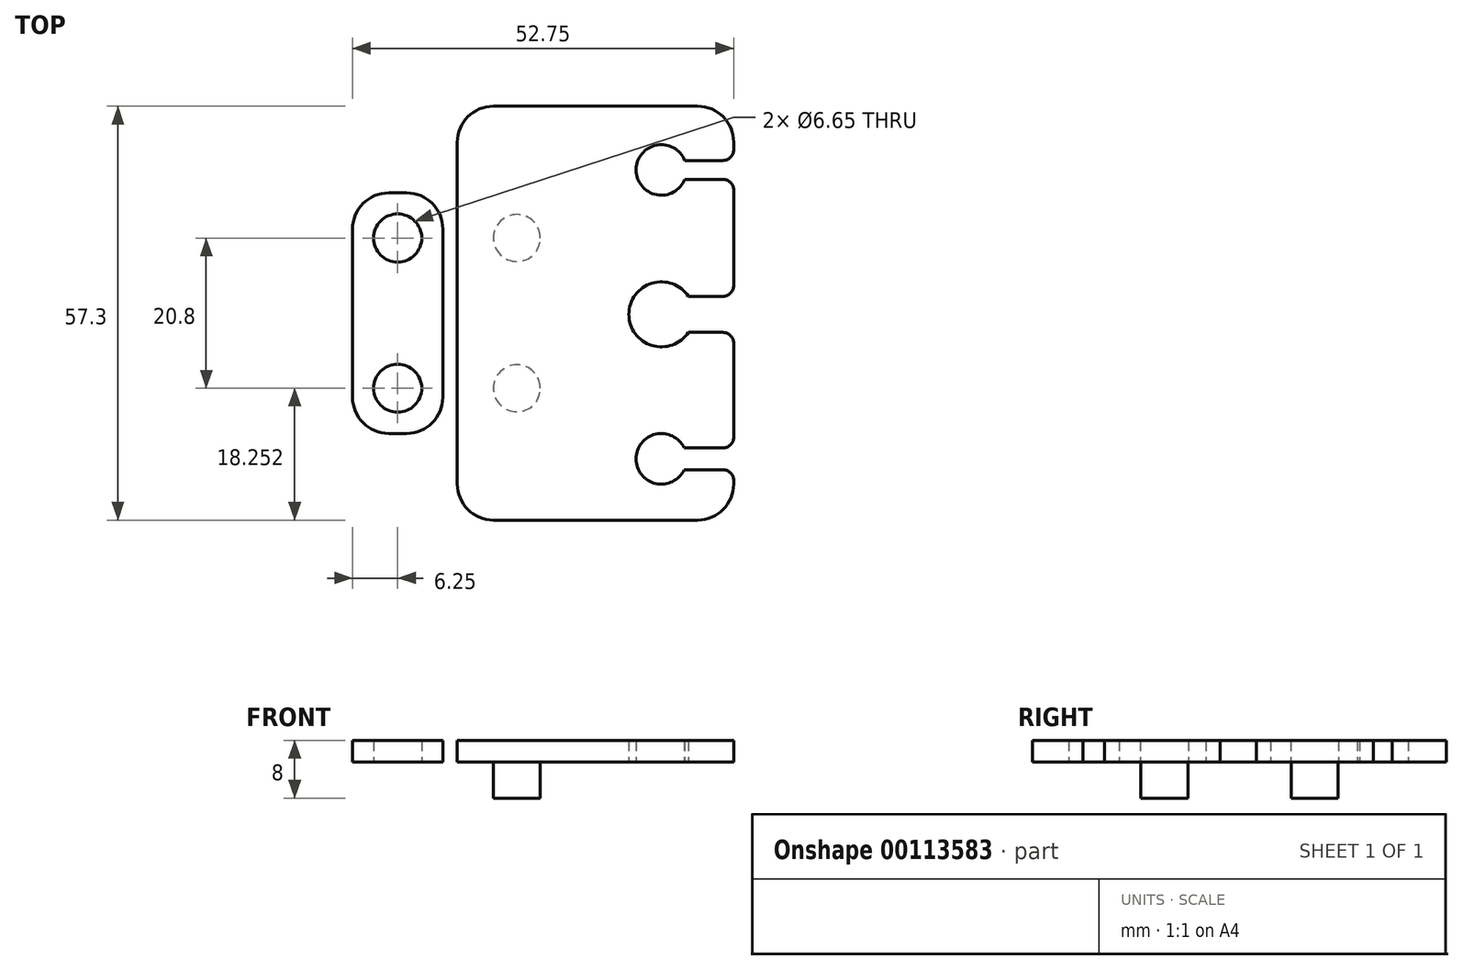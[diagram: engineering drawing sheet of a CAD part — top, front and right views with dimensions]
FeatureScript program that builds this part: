
annotation { "Feature Type Name" : "Feature", "Feature Type Description" : "" }
export const myFeature = defineFeature(function(context is Context, id is Id, definition is map)
    precondition{}
    {
        {
            var Q0;
            Q0=qCreatedBy(makeId("Top.planeOp"),FACE);
            var sketch = newSketch(context, id + "F0", { "sketchPlane" : qUnion([Q0])});
            skCircle(sketch, "E0", {"center": v(0, 10.57) * mm, "radius": 3.25 * mm});
            skCircle(sketch, "E1", {"center": v(0, -10.23) * mm, "radius": 3.25 * mm});
            skLineSegment(sketch, "E2", {"start": v(10, 35.02) * mm, "end": v(10, -24.98) * mm, "construction": true});
            skLineSegment(sketch, "E3", {"start": v(-8.25, -28.48) * mm, "end": v(30, -28.48) * mm});
            skLineSegment(sketch, "E4", {"start": v(30, -28.48) * mm, "end": v(30, 28.82) * mm});
            skLineSegment(sketch, "E5", {"start": v(30, 28.82) * mm, "end": v(-8.25, 28.82) * mm});
            skLineSegment(sketch, "E6", {"start": v(-8.25, 28.82) * mm, "end": v(-8.25, -28.48) * mm});
            skCircle(sketch, "E7", {"center": v(20, 0) * mm, "radius": 4.5 * mm});
            skCircle(sketch, "E8.0.1.0", {"center": v(20, 20) * mm, "radius": 3.5 * mm});
            skLineSegment(sketch, "E8.direction2", {"start": v(20, 0) * mm, "end": v(20, 20) * mm, "construction": true});
            skLineSegment(sketch, "E9.direction2", {"start": v(20, 0) * mm, "end": v(20, -20) * mm, "construction": true});
            skCircle(sketch, "E10.MirrorC", {"center": v(-16.5, 10.57) * mm, "radius": 3.25 * mm});
            skCircle(sketch, "E11.MirrorC", {"center": v(-16.5, -10.23) * mm, "radius": 3.25 * mm});
            skLineSegment(sketch, "E12", {"start": v(-16.5, 16.82) * mm, "end": v(-10.25, 16.82) * mm});
            skLineSegment(sketch, "E13", {"start": v(-10.25, 16.82) * mm, "end": v(-10.25, -16.48) * mm});
            skLineSegment(sketch, "E14", {"start": v(-10.25, -16.48) * mm, "end": v(-16.5, -16.48) * mm});
            skLineSegment(sketch, "E15", {"start": v(-16.5, 10.57) * mm, "end": v(-16.5, -10.23) * mm, "construction": true});
            skLineSegment(sketch, "E16.MirrorCS", {"start": v(-16.5, 16.82) * mm, "end": v(-22.75, 16.82) * mm});
            skLineSegment(sketch, "E17.MirrorCS", {"start": v(-22.75, 16.82) * mm, "end": v(-22.75, -16.48) * mm});
            skLineSegment(sketch, "E18.MirrorCS", {"start": v(-22.75, -16.48) * mm, "end": v(-16.5, -16.48) * mm});
            skLineSegment(sketch, "E19", {"start": v(30, 20) * mm, "end": v(-8.25, 20) * mm, "construction": true});
            skLineSegment(sketch, "E20.MirrorCS", {"start": v(30, -20) * mm, "end": v(-8.25, -20) * mm, "construction": true});
            skLineSegment(sketch, "E21", {"start": v(23.74, 2.5) * mm, "end": v(30, 2.5) * mm});
            skLineSegment(sketch, "E22.MirrorCS", {"start": v(23.74, -2.5) * mm, "end": v(30, -2.5) * mm});
            skLineSegment(sketch, "E23", {"start": v(23.25, 21.3) * mm, "end": v(30, 21.3) * mm});
            skLineSegment(sketch, "E24.MirrorCS", {"start": v(23.25, 18.7) * mm, "end": v(30, 18.7) * mm});
            skCircle(sketch, "E25.MirrorC", {"center": v(20, -20) * mm, "radius": 3.5 * mm});
            skCircle(sketch, "E26.0", {"center": v(-16.5, 10.57) * mm, "radius": 3.33 * mm});
            skCircle(sketch, "E27.0", {"center": v(-16.5, -10.23) * mm, "radius": 3.33 * mm});
            skLineSegment(sketch, "E28", {"start": v(23.16, -18.5) * mm, "end": v(30, -18.5) * mm});
            skLineSegment(sketch, "E29.MirrorCS", {"start": v(23.16, -21.5) * mm, "end": v(30, -21.5) * mm});
            skSolve(sketch);
        }
        {
            var Q0;
            Q0=makeQuery(id+"F0.imprint","IMPRINT",FACE,{"disambiguationData":[TD([[makeQuery(id+"F0.imprint","IMPRINT",EDGE,{"derivedFrom":sQuery(id+"F0.wireOp",EDGE,"E0")}),-1.0]])]});
            var Q1;
            Q1=makeQuery(id+"F0.imprint","IMPRINT",FACE,{"disambiguationData":[TD([[makeQuery(id+"F0.imprint","IMPRINT",EDGE,{"derivedFrom":sQuery(id+"F0.wireOp",EDGE,"E0")}),1.0]])]});
            var Q2;
            Q2=makeQuery(id+"F0.imprint","IMPRINT",FACE,{"disambiguationData":[TD([[makeQuery(id+"F0.imprint","IMPRINT",EDGE,{"derivedFrom":sQuery(id+"F0.wireOp",EDGE,"E1")}),1.0]])]});
            extrude(context, id + "F1", {"entities" : qUnion([Q0, Q1, Q2]), "depth" : 3 * mm});
        }
        {
            var Q0;
            Q0=makeQuery(id+"F1.opExtrude","SWEPT_EDGE",EDGE,{"disambiguationData":[OSD([sQuery(id+"F0.wireOp",EDGE,"E5"),sQuery(id+"F0.wireOp",EDGE,"E6")])]});
            var Q1;
            Q1=makeQuery(id+"F1.opExtrude","SWEPT_EDGE",EDGE,{"disambiguationData":[OSD([sQuery(id+"F0.wireOp",EDGE,"E3"),sQuery(id+"F0.wireOp",EDGE,"E6")])]});
            var Q2;
            Q2=makeQuery(id+"F1.opExtrude","SWEPT_EDGE",EDGE,{"disambiguationData":[OSD([sQuery(id+"F0.wireOp",EDGE,"E3"),sQuery(id+"F0.wireOp",EDGE,"E4")])]});
            var Q3;
            Q3=makeQuery(id+"F1.opExtrude","SWEPT_EDGE",EDGE,{"disambiguationData":[OSD([sQuery(id+"F0.wireOp",EDGE,"E4"),sQuery(id+"F0.wireOp",EDGE,"E5")])]});
            fillet(context, id + "F2", {"entities" : qUnion([Q0, Q1, Q2, Q3]), "radius" : 5 * mm, "tangentPropagation" : true, "allowEdgeOverflow" : false});
        }
        {
            var Q0;
            Q0=makeQuery(id+"F0.imprint","IMPRINT",FACE,{"disambiguationData":[TD([[makeQuery(id+"F0.imprint","IMPRINT",EDGE,{"derivedFrom":sQuery(id+"F0.wireOp",EDGE,"E0")}),1.0]])]});
            var Q1;
            Q1=makeQuery(id+"F0.imprint","IMPRINT",FACE,{"disambiguationData":[TD([[makeQuery(id+"F0.imprint","IMPRINT",EDGE,{"derivedFrom":sQuery(id+"F0.wireOp",EDGE,"E1")}),1.0]])]});
            extrude(context, id + "F3", {"entities" : qUnion([Q0, Q1]), "operationType" : NewBodyOperationType.ADD, "oppositeDirection" : true, "depth" : 5 * mm});
        }
        {
            var Q0;
            Q0=makeQuery(id+"F0.imprint","IMPRINT",FACE,{"disambiguationData":[TD([[makeQuery(id+"F0.imprint","IMPRINT",EDGE,{"derivedFrom":sQuery(id+"F0.wireOp",EDGE,"E12")}),-1.0]])]});
            extrude(context, id + "F4", {"entities" : qUnion([Q0]), "depth" : 3 * mm});
        }
        {
            var Q0;
            Q0=makeQuery(id+"F4.opExtrude","SWEPT_EDGE",EDGE,{"disambiguationData":[OSD([sQuery(id+"F0.wireOp",EDGE,"E16.MirrorCS"),sQuery(id+"F0.wireOp",EDGE,"E17.MirrorCS")])]});
            var Q1;
            Q1=makeQuery(id+"F4.opExtrude","SWEPT_EDGE",EDGE,{"disambiguationData":[OSD([sQuery(id+"F0.wireOp",EDGE,"E17.MirrorCS"),sQuery(id+"F0.wireOp",EDGE,"E18.MirrorCS")])]});
            var Q2;
            Q2=makeQuery(id+"F4.opExtrude","SWEPT_EDGE",EDGE,{"disambiguationData":[OSD([sQuery(id+"F0.wireOp",EDGE,"E12"),sQuery(id+"F0.wireOp",EDGE,"E13")])]});
            var Q3;
            Q3=makeQuery(id+"F4.opExtrude","SWEPT_EDGE",EDGE,{"disambiguationData":[OSD([sQuery(id+"F0.wireOp",EDGE,"E13"),sQuery(id+"F0.wireOp",EDGE,"E14")])]});
            fillet(context, id + "F5", {"entities" : qUnion([Q0, Q1, Q2, Q3]), "radius" : 5 * mm, "tangentPropagation" : true, "allowEdgeOverflow" : false});
        }
        {
            var Q0;
            Q0=makeQuery(id+"F1.opExtrude","SWEPT_EDGE",EDGE,{"disambiguationData":[OSD([sQuery(id+"F0.wireOp",EDGE,"E4"),sQuery(id+"F0.wireOp",EDGE,"73de7699-7821-4ff2-8a54-5b59328dcf0b0.MirrorCS")])]});
            var Q1;
            Q1=makeQuery(id+"F1.opExtrude","SWEPT_EDGE",EDGE,{"disambiguationData":[OSD([sQuery(id+"F0.wireOp",EDGE,"E4"),sQuery(id+"F0.wireOp",EDGE,"9f41aabc-ced6-495f-9977-c08cf494d5910.MirrorCS")])]});
            var Q2;
            Q2=makeQuery(id+"F1.opExtrude","SWEPT_EDGE",EDGE,{"disambiguationData":[OSD([sQuery(id+"F0.wireOp",EDGE,"E4"),sQuery(id+"F0.wireOp",EDGE,"E22.MirrorCS")])]});
            var Q3;
            Q3=makeQuery(id+"F1.opExtrude","SWEPT_EDGE",EDGE,{"disambiguationData":[OSD([sQuery(id+"F0.wireOp",EDGE,"E4"),sQuery(id+"F0.wireOp",EDGE,"E21")])]});
            var Q4;
            Q4=makeQuery(id+"F1.opExtrude","SWEPT_EDGE",EDGE,{"disambiguationData":[OSD([sQuery(id+"F0.wireOp",EDGE,"E4"),sQuery(id+"F0.wireOp",EDGE,"E24.MirrorCS")])]});
            var Q5;
            Q5=makeQuery(id+"F1.opExtrude","SWEPT_EDGE",EDGE,{"disambiguationData":[OSD([sQuery(id+"F0.wireOp",EDGE,"E4"),sQuery(id+"F0.wireOp",EDGE,"E23")])]});
            fillet(context, id + "F6", {"entities" : qUnion([Q0, Q1, Q2, Q3, Q4, Q5]), "radius" : 1.5 * mm, "tangentPropagation" : true, "allowEdgeOverflow" : false});
        }
    });
